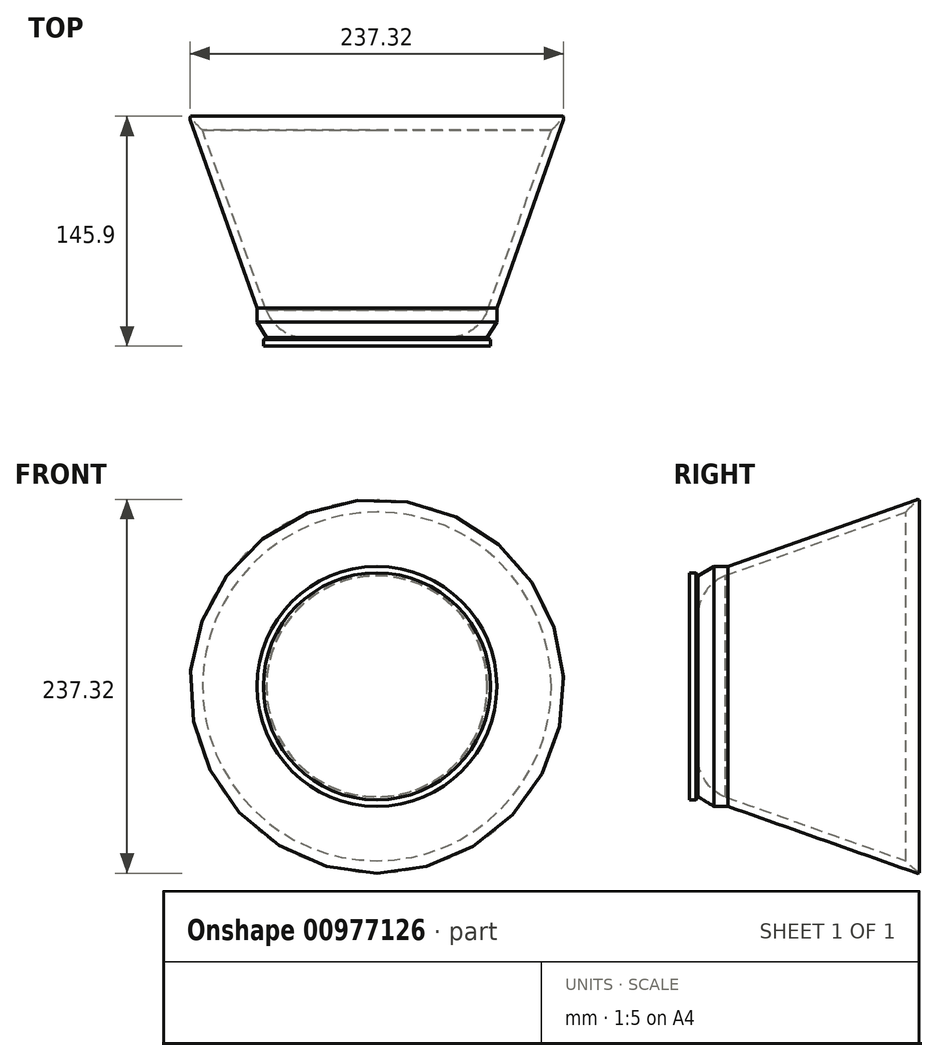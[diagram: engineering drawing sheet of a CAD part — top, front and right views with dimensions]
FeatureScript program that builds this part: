
annotation { "Feature Type Name" : "Feature", "Feature Type Description" : "" }
export const myFeature = defineFeature(function(context is Context, id is Id, definition is map)
    precondition{}
    {
        {
            var Q0;
            Q0=qCreatedBy(makeId("Top.planeOp"),FACE);
            var sketch = newSketch(context, id + "F0", { "sketchPlane" : qUnion([Q0])});
            skLineSegment(sketch, "E0", {"start": v(-76.2, 24.2) * mm, "end": v(-118.53, 143.93) * mm});
            skLineSegment(sketch, "E1", {"start": v(-110.76, 137.2) * mm, "end": v(-70.32, 22.8) * mm});
            skLineSegment(sketch, "E2", {"start": v(-62.26, 0) * mm, "end": v(-63.3, 0) * mm});
            skLineSegment(sketch, "E3.top", {"start": v(-72.1, 0) * mm, "end": v(-67.65, 0) * mm});
            skLineSegment(sketch, "E3.left", {"start": v(-76.2, 24.2) * mm, "end": v(-76.2, 15.3) * mm});
            skLineSegment(sketch, "E3.right", {"start": v(0, 5.08) * mm, "end": v(0, 0) * mm});
            skLineSegment(sketch, "E4.trimOffspring", {"start": v(-62.26, 0) * mm, "end": v(-21.51, 0) * mm});
            skLineSegment(sketch, "E5", {"start": v(0, 0) * mm, "end": v(0, 5.08) * mm});
            skArc(sketch, "E6", {"start": v(-118.32, 145.9) * mm, "mid": v(-114.88, 141.25) * mm, "end": v(-110.76, 137.2) * mm});
            skPoint(sketch, "E7.start.orphan", {"position": v(-116.36, 153.03) * mm});
            skPoint(sketch, "E8.orphan", {"position": v(-121.75, 153.03) * mm});
            skPoint(sketch, "E9.orphan", {"position": v(0, 23.42) * mm});
            skLineSegment(sketch, "E10.trimOffspring", {"start": v(-13.89, 0) * mm, "end": v(0, 0) * mm});
            skLineSegment(sketch, "E11", {"start": v(-44.96, 5.27) * mm, "end": v(0, 5.08) * mm});
            skPoint(sketch, "E12.orphan", {"position": v(0, 13.35) * mm});
            skArc(sketch, "E13", {"start": v(-70.32, 22.8) * mm, "mid": v(-60.35, 10.1) * mm, "end": v(-44.96, 5.27) * mm});
            skArc(sketch, "E14", {"start": v(-118.32, 145.9) * mm, "mid": v(-118.65, 144.94) * mm, "end": v(-118.53, 143.93) * mm});
            skPoint(sketch, "E15.center.orphan", {"position": v(-118.53, 145.84) * mm});
            skLineSegment(sketch, "E16", {"start": v(-76.2, 15.3) * mm, "end": v(-70.07, 5.28) * mm});
            skLineSegment(sketch, "E17", {"start": v(-70.07, 5.28) * mm, "end": v(-72.1, 4.04) * mm});
            skLineSegment(sketch, "E18", {"start": v(-72.1, 4.04) * mm, "end": v(-72.1, 0) * mm});
            skLineSegment(sketch, "E19", {"start": v(-72.1, 0) * mm, "end": v(0, 0) * mm});
            skPoint(sketch, "E20.end.orphan", {"position": v(-67.65, -1.7) * mm});
            skPoint(sketch, "E21.start.orphan", {"position": v(-63.3, -1.7) * mm});
            skPoint(sketch, "E22.start.orphan", {"position": v(-21.51, -1.7) * mm});
            skPoint(sketch, "E23.1.0.1.start.orphan", {"position": v(-13.89, -1.7) * mm});
            skSolve(sketch);
        }
        {
            var Q0;
            Q0=makeQuery(id+"F0.imprint","IMPRINT",FACE,{"disambiguationData":[TD([[makeQuery(id+"F0.imprint","IMPRINT",EDGE,{"derivedFrom":sQuery(id+"F0.wireOp",EDGE,"E0")}),-1.0]])]});
            var Q1;
            Q1=sQuery(id+"F0.wireOp",EDGE,"E5");
            revolve(context, id + "F1", {"surfaceOperationType" : NewSurfaceOperationType.NEW, "entities" : qUnion([Q0]), "axis" : qUnion([Q1]), "revolveType" : RevolveType.FULL});
        }
    });
